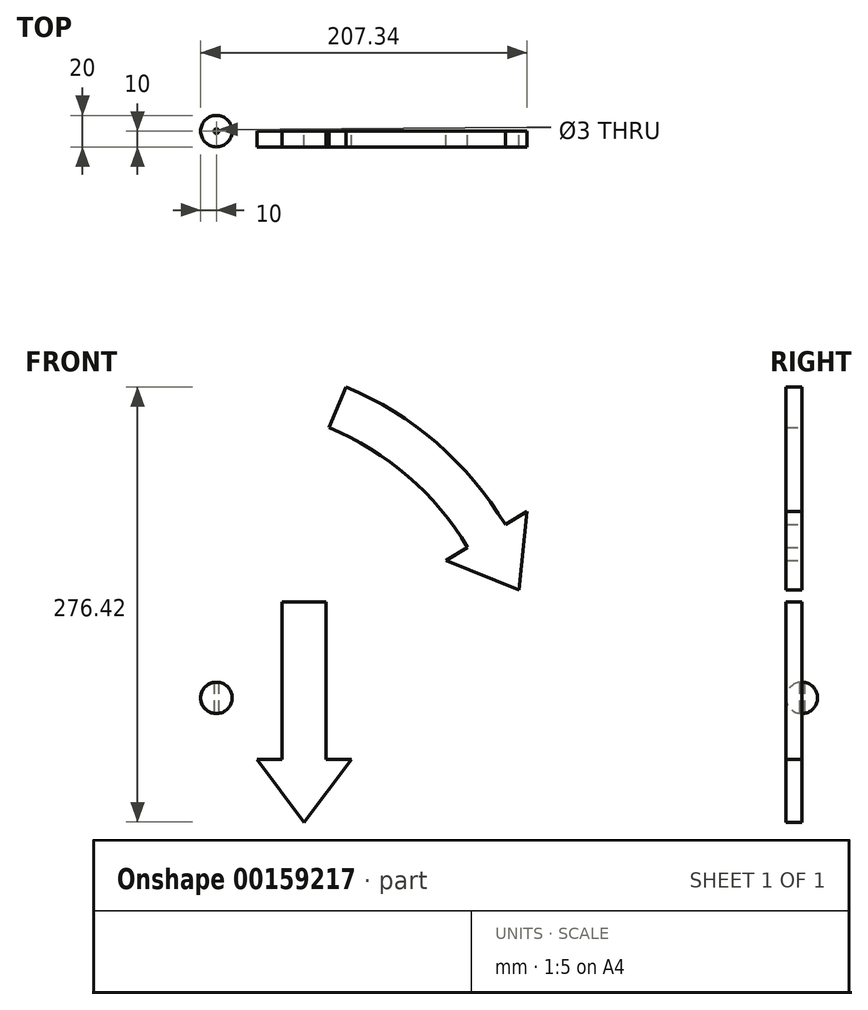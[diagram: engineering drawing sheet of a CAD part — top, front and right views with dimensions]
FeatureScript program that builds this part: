
annotation { "Feature Type Name" : "Feature", "Feature Type Description" : "" }
export const myFeature = defineFeature(function(context is Context, id is Id, definition is map)
    precondition{}
    {
        {
            var Q0;
            Q0=qCreatedBy(makeId("Front.planeOp"),FACE);
            var sketch = newSketch(context, id + "F0", { "sketchPlane" : qUnion([Q0])});
            skLineSegment(sketch, "E0", {"start": v(0, 0) * mm, "end": v(0, 20) * mm});
            skArc(sketch, "E1", {"start": v(0, 0) * mm, "mid": v(10, 10) * mm, "end": v(0, 20) * mm});
            skLineSegment(sketch, "E2", {"start": v(1.5, 19.89) * mm, "end": v(1.5, 0.11) * mm});
            skLineSegment(sketch, "E3", {"start": v(197.34, 128.3) * mm, "end": v(192.07, 78.59) * mm});
            skLineSegment(sketch, "E4", {"start": v(192.07, 78.59) * mm, "end": v(171.54, 112.84) * mm, "construction": true});
            skLineSegment(sketch, "E5", {"start": v(197.34, 128.3) * mm, "end": v(171.54, 112.84) * mm});
            skArc(sketch, "E6", {"start": v(171.54, 112.84) * mm, "mid": v(130.8, 161.3) * mm, "end": v(76.98, 194.6) * mm, "construction": true});
            skLineSegment(sketch, "E7.MirrorCS", {"start": v(145.73, 97.36) * mm, "end": v(171.54, 112.84) * mm});
            skLineSegment(sketch, "E8.MirrorCS", {"start": v(145.73, 97.36) * mm, "end": v(192.07, 78.59) * mm});
            skArc(sketch, "E9.0", {"start": v(183.54, 120.04) * mm, "mid": v(139.97, 171.88) * mm, "end": v(82.37, 207.51) * mm});
            skArc(sketch, "E10.0", {"start": v(159.53, 105.64) * mm, "mid": v(121.65, 150.7) * mm, "end": v(71.6, 181.67) * mm});
            skLineSegment(sketch, "E11", {"start": v(71.6, 181.67) * mm, "end": v(82.37, 207.51) * mm});
            skLineSegment(sketch, "E12", {"start": v(41.75, 71.02) * mm, "end": v(41.75, -28.98) * mm});
            skLineSegment(sketch, "E13", {"start": v(41.75, -28.98) * mm, "end": v(25.66, -28.98) * mm});
            skLineSegment(sketch, "E14", {"start": v(25.66, -28.98) * mm, "end": v(55.75, -68.91) * mm});
            skLineSegment(sketch, "E15", {"start": v(55.75, 71.02) * mm, "end": v(41.75, 71.02) * mm});
            skLineSegment(sketch, "E16", {"start": v(55.75, -68.91) * mm, "end": v(55.75, 71.02) * mm, "construction": true});
            skLineSegment(sketch, "E17.MirrorCS", {"start": v(55.75, 71.02) * mm, "end": v(69.75, 71.02) * mm});
            skLineSegment(sketch, "E18.MirrorCS", {"start": v(69.75, 71.02) * mm, "end": v(69.75, -28.98) * mm});
            skLineSegment(sketch, "E19.MirrorCS", {"start": v(69.75, -28.98) * mm, "end": v(85.84, -28.98) * mm});
            skLineSegment(sketch, "E20.MirrorCS", {"start": v(85.84, -28.98) * mm, "end": v(55.75, -68.91) * mm});
            skSolve(sketch);
        }
        {
            var Q0;
            {var subQ0=sQuery(id+"F0.wireOp",EDGE,"E2");Q0=makeQuery(id+"F0.imprint","IMPRINT",FACE,{"disambiguationData":[TD([[makeQuery(id+"F0.imprint","IMPRINT",EDGE,{"derivedFrom":subQ0}),1.0]])]});}
            var Q1;
            Q1=sQuery(id+"F0.wireOp",EDGE,"E0");
            revolve(context, id + "F1", {"entities" : qUnion([Q0]), "axis" : qUnion([Q1]), "revolveType" : RevolveType.FULL});
        }
        {
            var Q0;
            {var subQ1=sQuery(id+"F0.wireOp",EDGE,"E9.0");Q0=makeQuery(id+"F0.imprint","IMPRINT",FACE,{"disambiguationData":[TD([[makeQuery(id+"F0.imprint","IMPRINT",EDGE,{"derivedFrom":subQ1}),1.0]])]});}
            var Q1;
            {var subQ6=sQuery(id+"F0.wireOp",EDGE,"E3");Q1=makeQuery(id+"F0.imprint","IMPRINT",FACE,{"disambiguationData":[TD([[makeQuery(id+"F0.imprint","IMPRINT",EDGE,{"derivedFrom":subQ6}),-1.0]])]});}
            var Q2;
            Q2=makeQuery(id+"F0.imprint","IMPRINT",FACE,{"disambiguationData":[TD([[makeQuery(id+"F0.imprint","IMPRINT",EDGE,{"derivedFrom":sQuery(id+"F0.wireOp",EDGE,"E12")}),1.0]])]});
            extrude(context, id + "F2", {"entities" : qUnion([Q0, Q1, Q2]), "depth" : 10 * mm});
        }
    });
